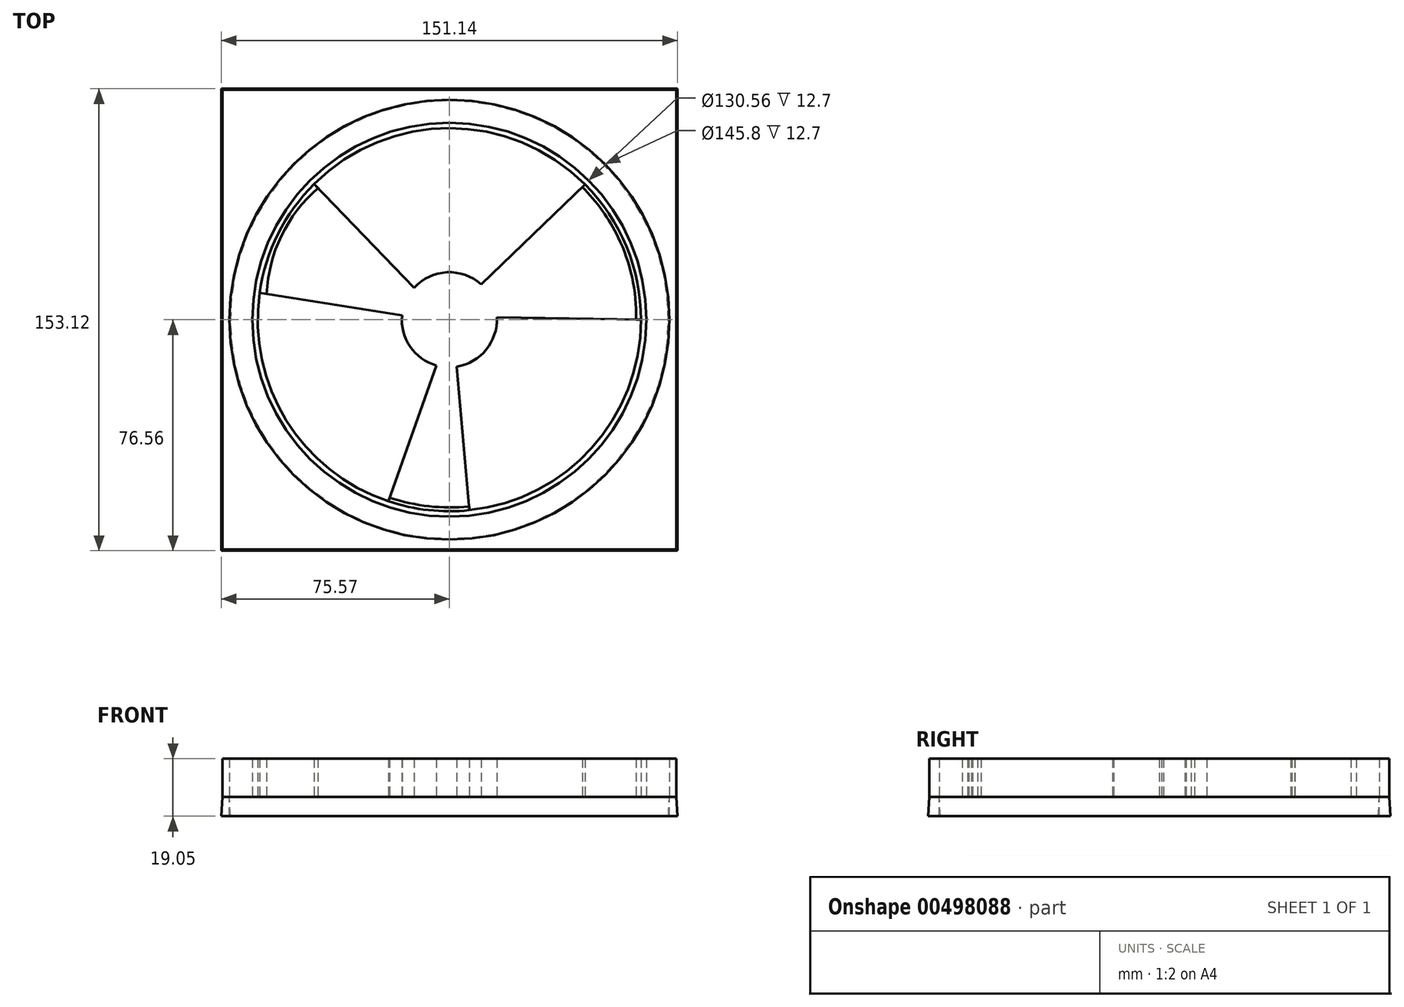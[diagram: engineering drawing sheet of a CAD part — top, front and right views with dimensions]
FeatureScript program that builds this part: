
annotation { "Feature Type Name" : "Feature", "Feature Type Description" : "" }
export const myFeature = defineFeature(function(context is Context, id is Id, definition is map)
    precondition{}
    {
        {
            var Q0;
            Q0=qCreatedBy(makeId("Top.planeOp"),FACE);
            var sketch = newSketch(context, id + "F0", { "sketchPlane" : qUnion([Q0])});
            skCircle(sketch, "E0", {"center": v(0, 0) * mm, "radius": 63.5 * mm});
            skCircle(sketch, "E1", {"center": v(0, 0) * mm, "radius": 65.28 * mm});
            skCircle(sketch, "E2", {"center": v(0, 0) * mm, "radius": 72.9 * mm});
            skArc(sketch, "E3", {"start": v(10.58, 11.65) * mm, "mid": v(10.57, 11.66) * mm, "end": v(10.57, 11.66) * mm});
            skLineSegment(sketch, "E4", {"start": v(-11.65, 10.58) * mm, "end": v(-11.65, 10.58) * mm});
            skLineSegment(sketch, "E5", {"start": v(-11.65, 10.58) * mm, "end": v(-44.82, 44.98) * mm});
            skLineSegment(sketch, "E6.2.0", {"start": v(10.57, 11.66) * mm, "end": v(44.94, 44.86) * mm});
            skLineSegment(sketch, "E6.3.0", {"start": v(15.72, 0.78) * mm, "end": v(63.5, -0.03) * mm});
            skLineSegment(sketch, "E7.1.0", {"start": v(2.43, -15.55) * mm, "end": v(6.66, -63.15) * mm});
            skLineSegment(sketch, "E8.2.0", {"start": v(-4.25, -15.15) * mm, "end": v(-20.2, -60.2) * mm});
            skLineSegment(sketch, "E9.2.0", {"start": v(-15.67, 1.42) * mm, "end": v(-62.87, 8.91) * mm});
            skArc(sketch, "E10", {"start": v(-15.67, 1.42) * mm, "mid": v(-12.96, -8.93) * mm, "end": v(-4.25, -15.15) * mm});
            skArc(sketch, "E11.trimOffspring", {"start": v(10.58, 11.65) * mm, "mid": v(-0.76, 15.72) * mm, "end": v(-11.65, 10.58) * mm});
            skArc(sketch, "E12.trimOffspring", {"start": v(2.43, -15.55) * mm, "mid": v(12.2, -9.93) * mm, "end": v(15.72, 0.78) * mm});
            skArc(sketch, "E13", {"start": v(-19.78, -59) * mm, "mid": v(-6.77, -61.86) * mm, "end": v(6.55, -61.88) * mm});
            skArc(sketch, "E14.trimOffspring", {"start": v(55.9, 27.34) * mm, "mid": v(50.65, 36.15) * mm, "end": v(44.03, 43.98) * mm});
            skArc(sketch, "E15", {"start": v(-43.5, 43.6) * mm, "mid": v(-55.64, 27.83) * mm, "end": v(-60.52, 8.54) * mm});
            skArc(sketch, "E16", {"start": v(61.85, 0) * mm, "mid": v(60.53, 14.03) * mm, "end": v(55.9, 27.34) * mm});
            skSolve(sketch);
        }
        {
            var Q0;
            {var subQ0=sQuery(id+"F0.wireOp",EDGE,"E5");Q0=makeQuery(id+"F0.imprint","IMPRINT",FACE,{"disambiguationData":[TD([[makeQuery(id+"F0.imprint","IMPRINT",EDGE,{"derivedFrom":subQ0}),-1.0]])]});}
            var Q1;
            {var subQ0=sQuery(id+"F0.wireOp",EDGE,"E6.3.0");Q1=makeQuery(id+"F0.imprint","IMPRINT",FACE,{"disambiguationData":[TD([[makeQuery(id+"F0.imprint","IMPRINT",EDGE,{"derivedFrom":subQ0}),-1.0]])]});}
            var Q2;
            {var subQ0=sQuery(id+"F0.wireOp",EDGE,"E8.2.0");Q2=makeQuery(id+"F0.imprint","IMPRINT",FACE,{"disambiguationData":[TD([[makeQuery(id+"F0.imprint","IMPRINT",EDGE,{"derivedFrom":subQ0}),-1.0]])]});}
            extrude(context, id + "F1", {"entities" : qUnion([Q0, Q1, Q2]), "depth" : 12.7 * mm});
        }
        {
            var Q0;
            Q0=makeQuery(id+"F0.imprint","IMPRINT",FACE,{"disambiguationData":[TD([[makeQuery(id+"F0.imprint","IMPRINT",EDGE,{"derivedFrom":sQuery(id+"F0.wireOp",EDGE,"E1")}),-1.0]])]});
            extrude(context, id + "F2", {"entities" : qUnion([Q0]), "depth" : 12.7 * mm});
        }
        {
            var Q0;
            Q0=sQuery(id+"F0.wireOp",EDGE,"E0");
            var Q1;
            Q1=sQuery(id+"F0.wireOp",EDGE,"E13");
            extrude(context, id + "F3", {"bodyType" : ToolBodyType.SURFACE, "surfaceEntities" : qUnion([Q0, Q1]), "depth" : 12.7 * mm});
        }
        {
            var Q0;
            Q0=qCreatedBy(makeId("Top.planeOp"),FACE);
            var sketch = newSketch(context, id + "F4", { "sketchPlane" : qUnion([Q0])});
            skCircle(sketch, "E17", {"center": v(0, 0) * mm, "radius": 72.9 * mm});
            skSolve(sketch);
        }
        {
            var Q0;
            Q0 = qSketchRegion(id + "F4", true);
            extrude(context, id + "F5", {"entities" : qUnion([Q0]), "oppositeDirection" : true, "depth" : 6.35 * mm});
        }
        {
            var Q0;
            {var subQ0=sQuery(id+"F0.wireOp",EDGE,"E14.trimOffspring");Q0=makeQuery(id+"F0.imprint","IMPRINT",FACE,{"disambiguationData":[TD([[makeQuery(id+"F0.imprint","IMPRINT",EDGE,{"derivedFrom":subQ0}),-1.0]])]});}
            var Q1;
            {var subQ5=sQuery(id+"F0.wireOp",EDGE,"E15");Q1=makeQuery(id+"F0.imprint","IMPRINT",FACE,{"disambiguationData":[TD([[makeQuery(id+"F0.imprint","IMPRINT",EDGE,{"derivedFrom":subQ5}),-1.0]])]});}
            var Q2;
            {var subQ5=sQuery(id+"F0.wireOp",EDGE,"E13");Q2=makeQuery(id+"F0.imprint","IMPRINT",FACE,{"disambiguationData":[TD([[makeQuery(id+"F0.imprint","IMPRINT",EDGE,{"derivedFrom":subQ5}),-1.0]])]});}
            extrude(context, id + "F6", {"entities" : qUnion([Q0, Q1, Q2]), "depth" : 12.7 * mm});
        }
        {
            var Q0;
            Q0=qCreatedBy(makeId("Top.planeOp"),FACE);
            var sketch = newSketch(context, id + "F7", { "sketchPlane" : qUnion([Q0])});
            skLineSegment(sketch, "E18.bottom", {"start": v(75.24, -76.23) * mm, "end": v(-75.24, -76.23) * mm});
            skLineSegment(sketch, "E18.top", {"start": v(75.24, 76.23) * mm, "end": v(-75.24, 76.23) * mm});
            skLineSegment(sketch, "E18.left", {"start": v(75.24, -76.23) * mm, "end": v(75.24, 76.23) * mm});
            skLineSegment(sketch, "E18.right", {"start": v(-75.24, -76.23) * mm, "end": v(-75.24, 76.23) * mm});
            skPoint(sketch, "E18.middle", {"position": v(0, 0) * mm});
            skSolve(sketch);
        }
        {
            var Q0;
            Q0=makeQuery(id+"F7.imprint","IMPRINT",FACE,{"disambiguationData":[TD([[makeQuery(id+"F7.imprint","IMPRINT",EDGE,{"derivedFrom":sQuery(id+"F7.wireOp",EDGE,"E18.bottom")}),-1.0]])]});
            var sketch = newSketch(context, id + "F8", { "sketchPlane" : qUnion([Q0])});
            skCircle(sketch, "E19", {"center": v(0, 0) * mm, "radius": 72.9 * mm});
            skSolve(sketch);
        }
        {
            var Q0;
            Q0=makeQuery(id+"F8.imprint","IMPRINT",FACE,{"disambiguationData":[TD([[makeQuery(id+"F8.imprint","IMPRINT",EDGE,{"derivedFrom":sQuery(id+"F8.wireOp",EDGE,"E19")}),-1.0]])]});
            extrude(context, id + "F9", {"entities" : qUnion([Q0]), "depth" : 12.7 * mm});
        }
        {
            var Q0;
            Q0=makeQuery(id+"F3.opExtrude","SWEPT_BODY",BODY,{"disambiguationData":[OSD([sQuery(id+"F0.wireOp",EDGE,"E0")])]});
            deleteBodies(context, id + "F10", {"entities" : qUnion([Q0])});
        }
        {
            var Q0;
            Q0=makeQuery(id+"F3.opExtrude","SWEPT_BODY",BODY,{"disambiguationData":[OSD([sQuery(id+"F0.wireOp",EDGE,"E13")])]});
            deleteBodies(context, id + "F11", {"entities" : qUnion([Q0])});
        }
        {
            var Q0;
            Q0=makeQuery(id+"F9.opExtrude","CAP_FACE",FACE,{"disambiguationData":[OSD([sQuery(id+"F7.wireOp",EDGE,"E18.bottom"),sQuery(id+"F7.wireOp",EDGE,"E18.top"),sQuery(id+"F7.wireOp",EDGE,"E18.left"),sQuery(id+"F7.wireOp",EDGE,"E18.right"),sQuery(id+"F8.wireOp",EDGE,"E19")])],"isStart":true});
            extrude(context, id + "F12", {"entities" : qUnion([Q0]), "depth" : 6.35 * mm, "hasDraft" : true, "draftAngle" : 3 * degree});
        }
    });
